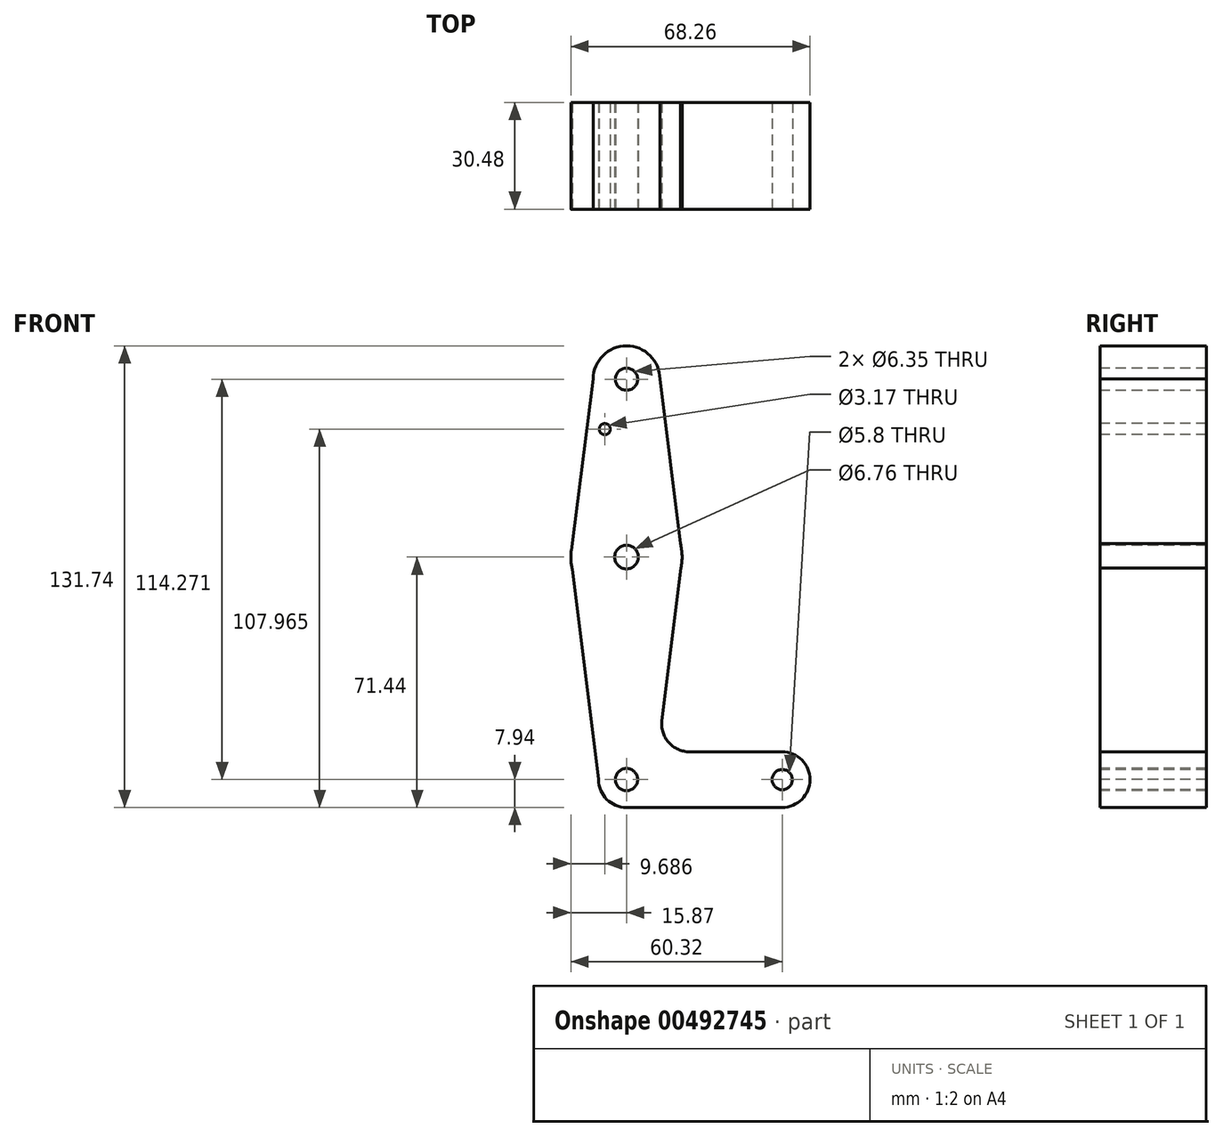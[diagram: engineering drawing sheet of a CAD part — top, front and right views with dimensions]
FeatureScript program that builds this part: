
annotation { "Feature Type Name" : "Feature", "Feature Type Description" : "" }
export const myFeature = defineFeature(function(context is Context, id is Id, definition is map)
    precondition{}
    {
        {
            var Q0;
            Q0=qCreatedBy(makeId("Front.planeOp"),FACE);
            var sketch = newSketch(context, id + "F0", { "sketchPlane" : qUnion([Q0])});
            skLineSegment(sketch, "E0", {"start": v(0, 114.27) * mm, "end": v(0, 0) * mm, "construction": true});
            skLineSegment(sketch, "E1", {"start": v(0, 0) * mm, "end": v(44.45, 0) * mm});
            skCircle(sketch, "E2", {"center": v(44.45, 0) * mm, "radius": 7.94 * mm});
            skCircle(sketch, "E3", {"center": v(0, 114.27) * mm, "radius": 9.53 * mm});
            skCircle(sketch, "E4", {"center": v(0, 0) * mm, "radius": 7.94 * mm});
            skCircle(sketch, "E5", {"center": v(0, 63.5) * mm, "radius": 15.88 * mm});
            skLineSegment(sketch, "E6", {"start": v(-9.52, 114.3) * mm, "end": v(-21.93, 114.3) * mm});
            skLineSegment(sketch, "E7", {"start": v(-7.94, 0) * mm, "end": v(-21.93, 0) * mm});
            skLineSegment(sketch, "E8", {"start": v(0, 114.27) * mm, "end": v(-9.52, 114.3) * mm});
            skLineSegment(sketch, "E9", {"start": v(0, 0) * mm, "end": v(-7.94, 0) * mm});
            skLineSegment(sketch, "E10", {"start": v(9.52, 114.3) * mm, "end": v(15.88, 63.5) * mm});
            skLineSegment(sketch, "E11", {"start": v(-9.52, 114.3) * mm, "end": v(-16, 63.5) * mm});
            skLineSegment(sketch, "E12", {"start": v(15.57, 60.42) * mm, "end": v(10.12, 16.88) * mm});
            skLineSegment(sketch, "E13", {"start": v(-15.5, 60.08) * mm, "end": v(-7.94, 0) * mm});
            skLineSegment(sketch, "E14", {"start": v(18, 7.94) * mm, "end": v(44.45, 7.94) * mm});
            skLineSegment(sketch, "E15", {"start": v(0, -7.94) * mm, "end": v(44.45, -7.94) * mm});
            skCircle(sketch, "E16", {"center": v(0, 114.27) * mm, "radius": 3.18 * mm});
            skCircle(sketch, "E17", {"center": v(0, 63.5) * mm, "radius": 3.38 * mm});
            skCircle(sketch, "E18", {"center": v(0, 0) * mm, "radius": 3.18 * mm});
            skCircle(sketch, "E19", {"center": v(44.45, 0) * mm, "radius": 2.9 * mm});
            skCircle(sketch, "E20", {"center": v(-6.18, 100.03) * mm, "radius": 1.59 * mm});
            skArc(sketch, "E21.filletArc", {"start": v(10.12, 16.88) * mm, "mid": v(12.04, 10.63) * mm, "end": v(18, 7.94) * mm});
            skSolve(sketch);
        }
        {
            var Q0;
            Q0 = qSketchRegion(id + "F0", true);
            extrude(context, id + "F1", {"entities" : qUnion([Q0]), "oppositeDirection" : true, "depth" : 30.48 * mm});
        }
    });
